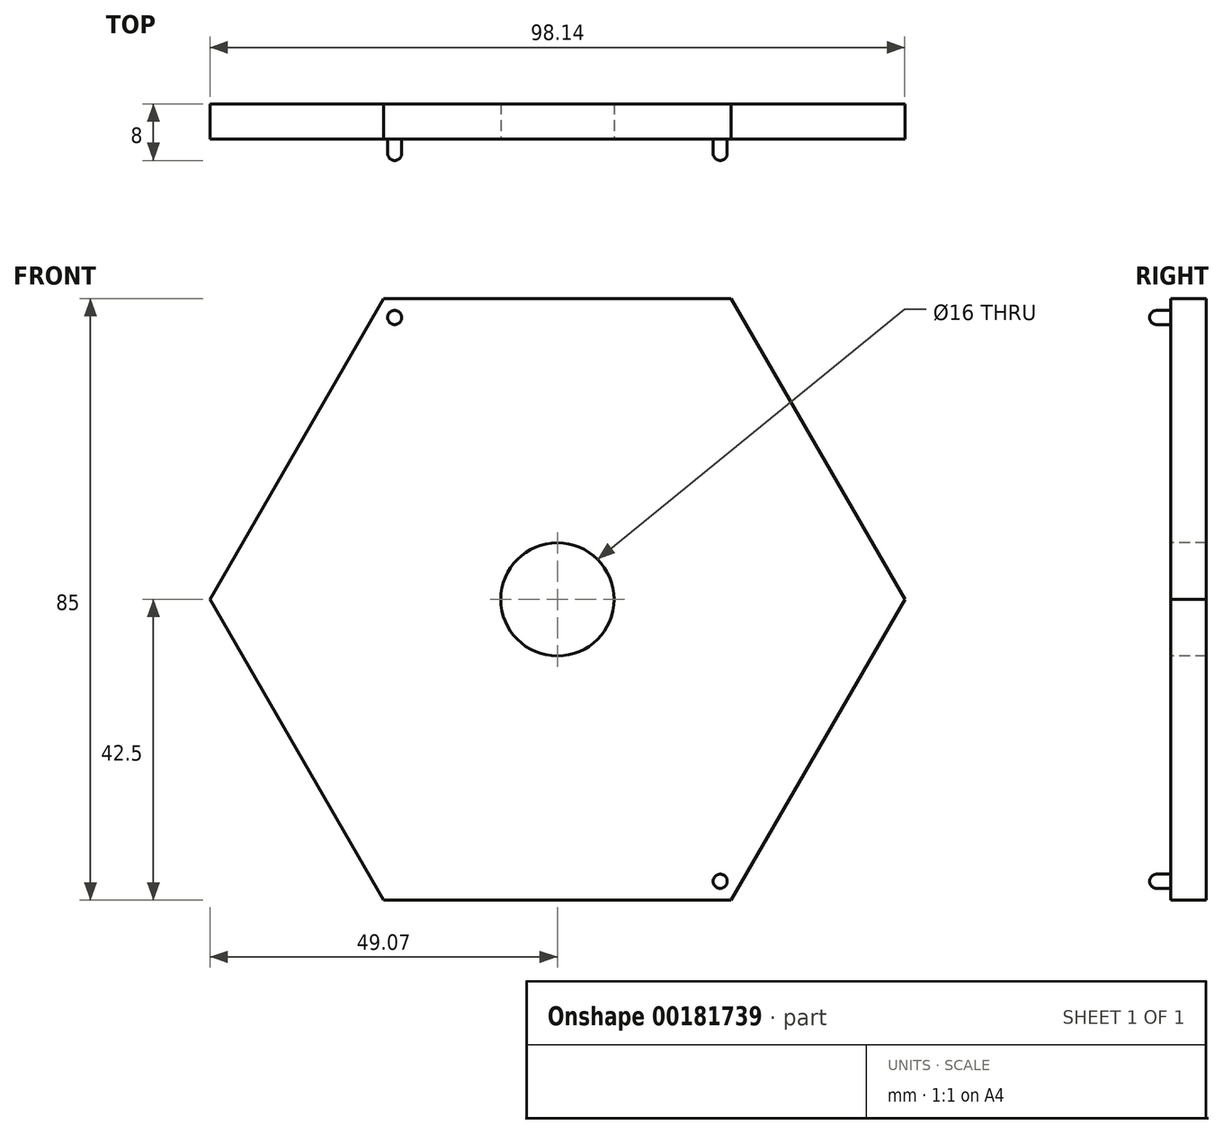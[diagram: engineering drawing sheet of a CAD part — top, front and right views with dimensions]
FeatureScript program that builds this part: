
annotation { "Feature Type Name" : "Feature", "Feature Type Description" : "" }
export const myFeature = defineFeature(function(context is Context, id is Id, definition is map)
    precondition{}
    {
        {
            var Q0;
            Q0=qCreatedBy(makeId("Front.planeOp"),FACE);
            var sketch = newSketch(context, id + "F0", { "sketchPlane" : qUnion([Q0])});
            skCircle(sketch, "E0.cCircle", {"center": v(0, 0) * mm, "radius": 42.5 * mm, "construction": true});
            skLineSegment(sketch, "E0.0", {"start": v(49.07, 0) * mm, "end": v(24.54, -42.5) * mm});
            skLineSegment(sketch, "E0.1", {"start": v(24.54, -42.5) * mm, "end": v(-24.54, -42.5) * mm});
            skLineSegment(sketch, "E0.2", {"start": v(-24.54, -42.5) * mm, "end": v(-49.07, 0) * mm});
            skLineSegment(sketch, "E0.3", {"start": v(-49.07, 0) * mm, "end": v(-24.54, 42.5) * mm});
            skLineSegment(sketch, "E0.4", {"start": v(-24.54, 42.5) * mm, "end": v(24.54, 42.5) * mm});
            skLineSegment(sketch, "E0.5", {"start": v(24.54, 42.5) * mm, "end": v(49.07, 0) * mm});
            skPoint(sketch, "E0.0.midPoint", {"position": v(36.8, -21.25) * mm});
            skSolve(sketch);
        }
        {
            var Q0;
            Q0 = qSketchRegion(id + "F0", true);
            extrude(context, id + "F1", {"entities" : qUnion([Q0]), "depth" : 5 * mm});
        }
        {
            var Q0;
            Q0=makeQuery(id+"F1.opExtrude","CAP_FACE",FACE,{"disambiguationData":[OSD([sQuery(id+"F0.wireOp",EDGE,"E0.0"),sQuery(id+"F0.wireOp",EDGE,"E0.1"),sQuery(id+"F0.wireOp",EDGE,"E0.2"),sQuery(id+"F0.wireOp",EDGE,"E0.3"),sQuery(id+"F0.wireOp",EDGE,"E0.4"),sQuery(id+"F0.wireOp",EDGE,"E0.5")])],"isStart":false});
            var sketch = newSketch(context, id + "F2", { "sketchPlane" : qUnion([Q0])});
            skCircle(sketch, "E1", {"center": v(0, 0) * mm, "radius": 8 * mm});
            skSolve(sketch);
        }
        {
            var Q0;
            Q0 = qSketchRegion(id + "F2", true);
            extrude(context, id + "F3", {"entities" : qUnion([Q0]), "operationType" : NewBodyOperationType.REMOVE, "oppositeDirection" : true, "depth" : 5 * mm});
        }
        {
            var Q0;
            Q0=makeQuery(id+"F1.opExtrude","CAP_FACE",FACE,{"disambiguationData":[OSD([sQuery(id+"F0.wireOp",EDGE,"E0.0"),sQuery(id+"F0.wireOp",EDGE,"E0.1"),sQuery(id+"F0.wireOp",EDGE,"E0.2"),sQuery(id+"F0.wireOp",EDGE,"E0.3"),sQuery(id+"F0.wireOp",EDGE,"E0.4"),sQuery(id+"F0.wireOp",EDGE,"E0.5")])],"isStart":false});
            var sketch = newSketch(context, id + "F4", { "sketchPlane" : qUnion([Q0])});
            skCircle(sketch, "E2.cCircle", {"center": v(0, 0) * mm, "radius": 37.5 * mm, "construction": true});
            skLineSegment(sketch, "E2.0", {"start": v(43.3, 0) * mm, "end": v(21.65, -37.5) * mm});
            skLineSegment(sketch, "E2.1", {"start": v(21.65, -37.5) * mm, "end": v(-21.65, -37.5) * mm});
            skLineSegment(sketch, "E2.2", {"start": v(-21.65, -37.5) * mm, "end": v(-43.3, 0) * mm});
            skLineSegment(sketch, "E2.3", {"start": v(-43.3, 0) * mm, "end": v(-21.65, 37.5) * mm});
            skLineSegment(sketch, "E2.4", {"start": v(-21.65, 37.5) * mm, "end": v(21.65, 37.5) * mm});
            skLineSegment(sketch, "E2.5", {"start": v(21.65, 37.5) * mm, "end": v(43.3, 0) * mm});
            skPoint(sketch, "E2.0.midPoint", {"position": v(32.48, -18.75) * mm});
            skSolve(sketch);
        }
        {
            var Q0;
            Q0=makeQuery(id+"F4.imprint","IMPRINT",FACE,{"disambiguationData":[TD([[makeQuery(id+"F4.imprint","IMPRINT",EDGE,{"derivedFrom":sQuery(id+"F4.wireOp",EDGE,"E2.0")}),1.0]])]});
            var sketch = newSketch(context, id + "F5", { "sketchPlane" : qUnion([Q0])});
            skCircle(sketch, "E3", {"center": v(-23, 39.82) * mm, "radius": 2.68 * mm});
            skCircle(sketch, "E4", {"center": v(23, -39.82) * mm, "radius": 2.68 * mm});
            skSolve(sketch);
        }
        {
            var Q0;
            Q0=makeQuery(id+"F4.imprint","IMPRINT",FACE,{"disambiguationData":[TD([[makeQuery(id+"F4.imprint","IMPRINT",EDGE,{"derivedFrom":sQuery(id+"F4.wireOp",EDGE,"E2.0")}),1.0]])]});
            var sketch = newSketch(context, id + "F6", { "sketchPlane" : qUnion([Q0])});
            skCircle(sketch, "E5", {"center": v(-23, 39.82) * mm, "radius": 1 * mm});
            skCircle(sketch, "E6.MirrorC", {"center": v(23, -39.82) * mm, "radius": 1 * mm});
            skSolve(sketch);
        }
        {
            var Q0;
            Q0 = qSketchRegion(id + "F6", true);
            extrude(context, id + "F7", {"entities" : qUnion([Q0]), "operationType" : NewBodyOperationType.ADD, "depth" : 3 * mm});
        }
        {
            var Q0;
            Q0=makeQuery(id+"F7.opExtrude","CAP_EDGE",EDGE,{"disambiguationData":[OSD([sQuery(id+"F6.wireOp",EDGE,"E5")])],"isStart":false});
            var Q1;
            Q1=makeQuery(id+"F7.opExtrude","CAP_EDGE",EDGE,{"disambiguationData":[OSD([sQuery(id+"F6.wireOp",EDGE,"E6.MirrorC")])],"isStart":false});
            fillet(context, id + "F8", {"entities" : qUnion([Q0, Q1]), "radius" : 1 * mm, "tangentPropagation" : true, "allowEdgeOverflow" : false});
        }
    });
